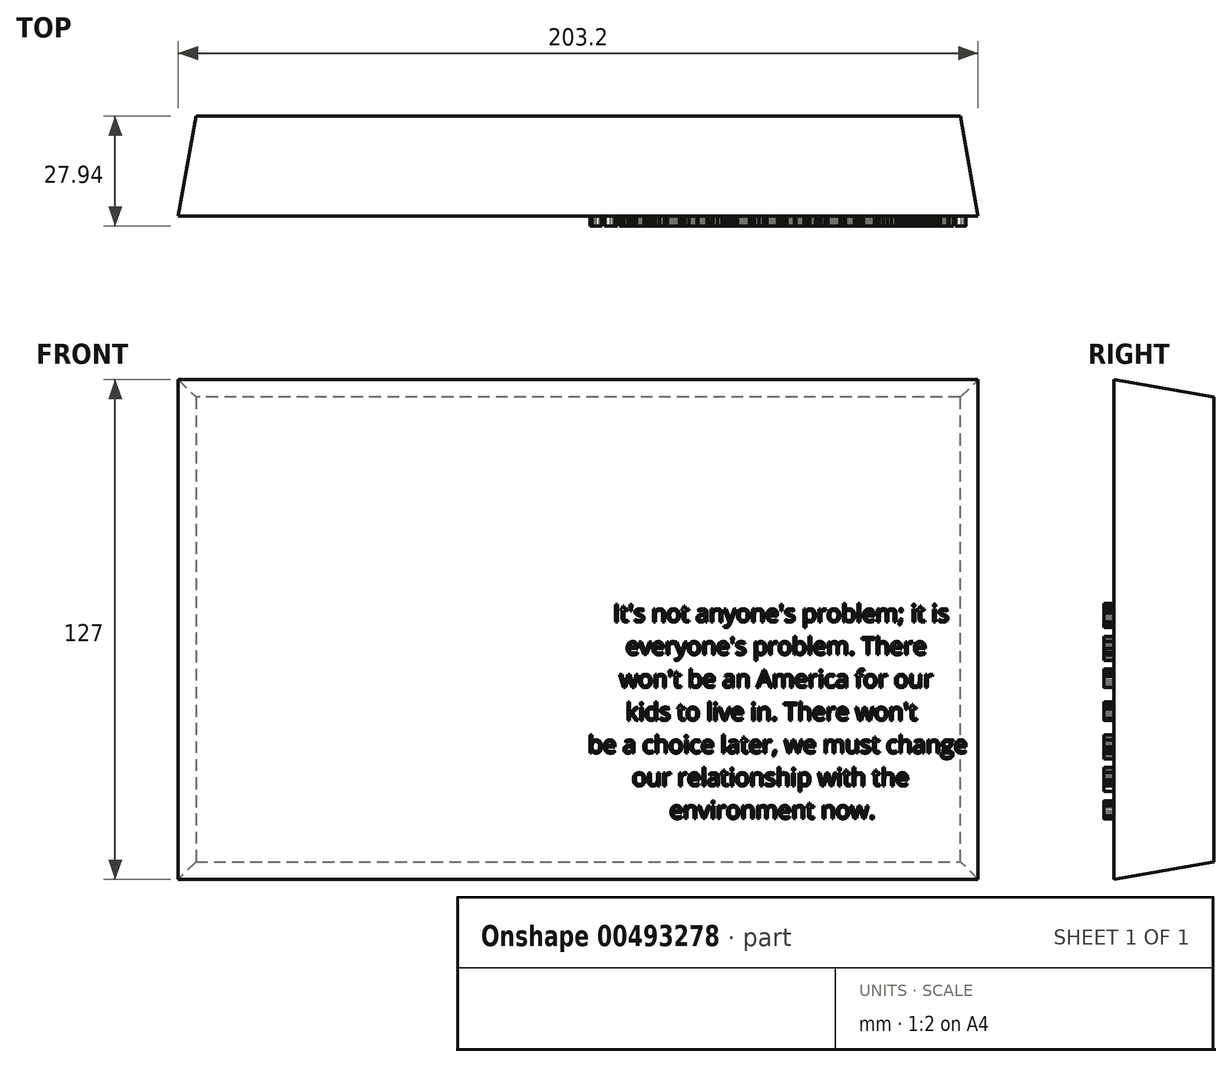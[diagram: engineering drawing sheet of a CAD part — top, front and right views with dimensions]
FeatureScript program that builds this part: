
annotation { "Feature Type Name" : "Feature", "Feature Type Description" : "" }
export const myFeature = defineFeature(function(context is Context, id is Id, definition is map)
    precondition{}
    {
        {
            var Q0;
            Q0=qCreatedBy(makeId("Front.planeOp"),FACE);
            var sketch = newSketch(context, id + "F0", { "sketchPlane" : qUnion([Q0])});
            skLineSegment(sketch, "E0.bottom", {"start": v(-203.2, 127) * mm, "end": v(0, 127) * mm});
            skLineSegment(sketch, "E0.top", {"start": v(-203.2, 0) * mm, "end": v(0, 0) * mm});
            skLineSegment(sketch, "E0.left", {"start": v(-203.2, 127) * mm, "end": v(-203.2, 0) * mm});
            skLineSegment(sketch, "E0.right", {"start": v(0, 127) * mm, "end": v(0, 0) * mm});
            skSolve(sketch);
        }
        {
            var Q0;
            Q0=qSketchRegion(id+"F0",true);
            extrude(context, id + "F1", {"entities" : qUnion([Q0]), "oppositeDirection" : true, "depth" : 25.4 * mm, "hasDraft" : true, "draftAngle" : 10 * degree, "draftPullDirection" : true});
        }
        {
            var Q0;
            Q0=makeQuery(id+"F1.opExtrude","CAP_FACE",FACE,{"disambiguationData":[OSD([sQuery(id+"F0.wireOp",EDGE,"E0.bottom"),sQuery(id+"F0.wireOp",EDGE,"E0.top"),sQuery(id+"F0.wireOp",EDGE,"E0.left"),sQuery(id+"F0.wireOp",EDGE,"E0.right")])],"isStart":true});
            var sketch = newSketch(context, id + "F2", { "sketchPlane" : qUnion([Q0])});
            skText(sketch, "E1", { "text": "    It\'s not anyone\'s problem; it is \n      everyone\'s problem. There\n     won\'t be an America for our \n      kids to live in. There won\'t\nbe a choice later, we must change\n       our relationship with the \n             environment now. ", "fontName": "OpenSans-Regular.ttf"});
            const initialGuessF2  = {"E1": [-0.09906, 0.06544, 1, 0, 0.00441]};
            skSetInitialGuess(sketch, initialGuessF2);
            skSolve(sketch);
        }
        {
            var Q0;
            Q0=qSketchRegion(id+"F2",true);
            extrude(context, id + "F3", {"entities" : qUnion([Q0]), "operationType" : NewBodyOperationType.ADD, "depth" : 2.54 * mm});
        }
    });
